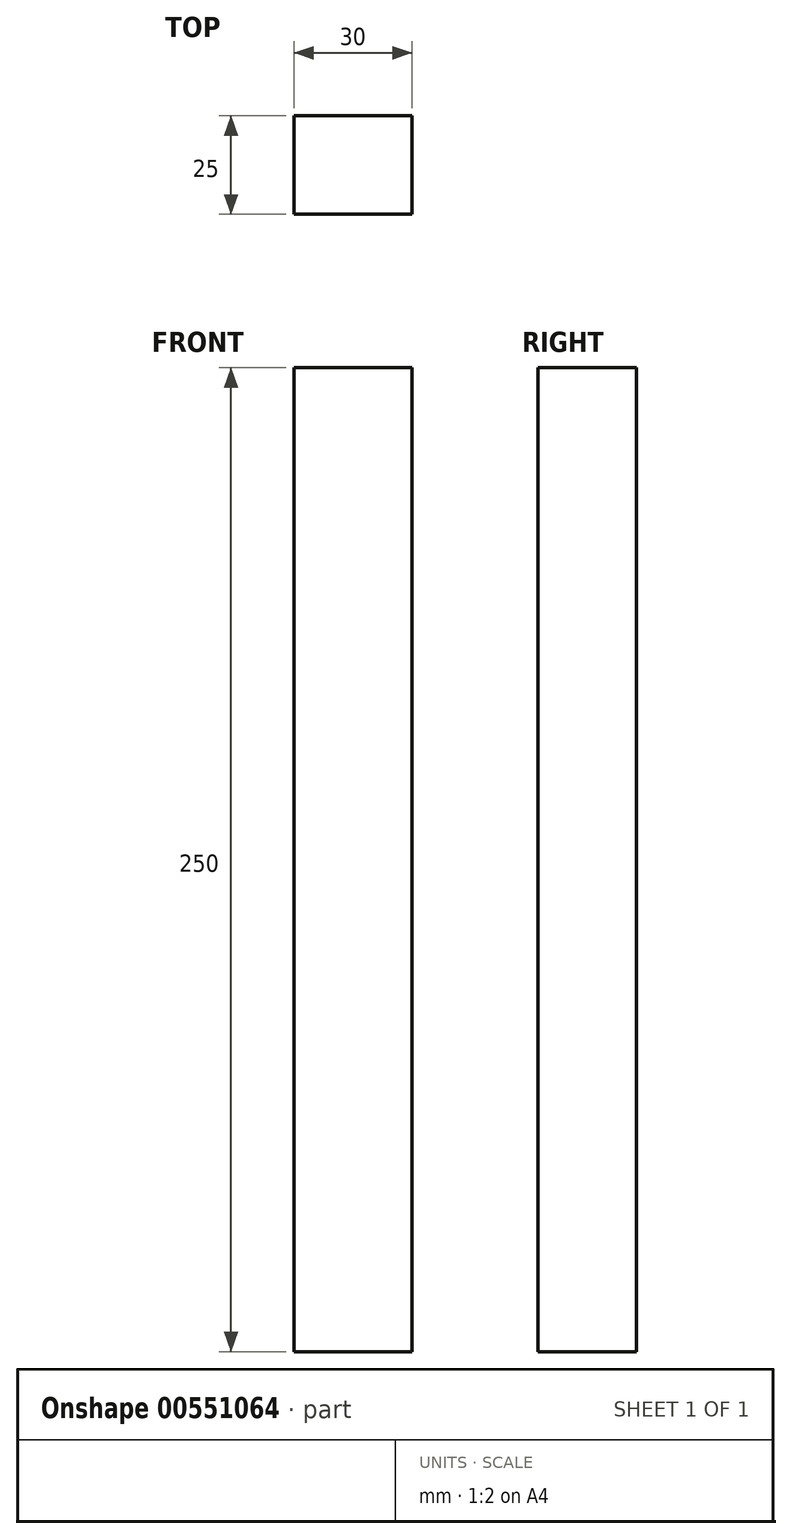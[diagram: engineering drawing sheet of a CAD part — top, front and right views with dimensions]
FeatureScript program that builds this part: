
annotation { "Feature Type Name" : "Feature", "Feature Type Description" : "" }
export const myFeature = defineFeature(function(context is Context, id is Id, definition is map)
    precondition{}
    {
        {
            var Q0;
            Q0=qCreatedBy(makeId("Front.planeOp"),FACE);
            var sketch = newSketch(context, id + "F0", { "sketchPlane" : qUnion([Q0])});
            skLineSegment(sketch, "E0", {"start": v(0, 0) * mm, "end": v(0, 250) * mm});
            skLineSegment(sketch, "E1", {"start": v(0, 250) * mm, "end": v(30, 250) * mm});
            skLineSegment(sketch, "E2", {"start": v(30, 250) * mm, "end": v(30, 0) * mm});
            skLineSegment(sketch, "E3", {"start": v(30, 0) * mm, "end": v(0, 0) * mm});
            skSolve(sketch);
        }
        {
            var Q0;
            Q0=makeQuery(id+"F0.imprint","IMPRINT",FACE,{"disambiguationData":[TD([[makeQuery(id+"F0.imprint","IMPRINT",EDGE,{"derivedFrom":sQuery(id+"F0.wireOp",EDGE,"E0")}),-1.0]])]});
            extrude(context, id + "F1", {"entities" : qUnion([Q0]), "depth" : 25 * mm, "offsetDistance" : 25 * mm});
        }
    });
